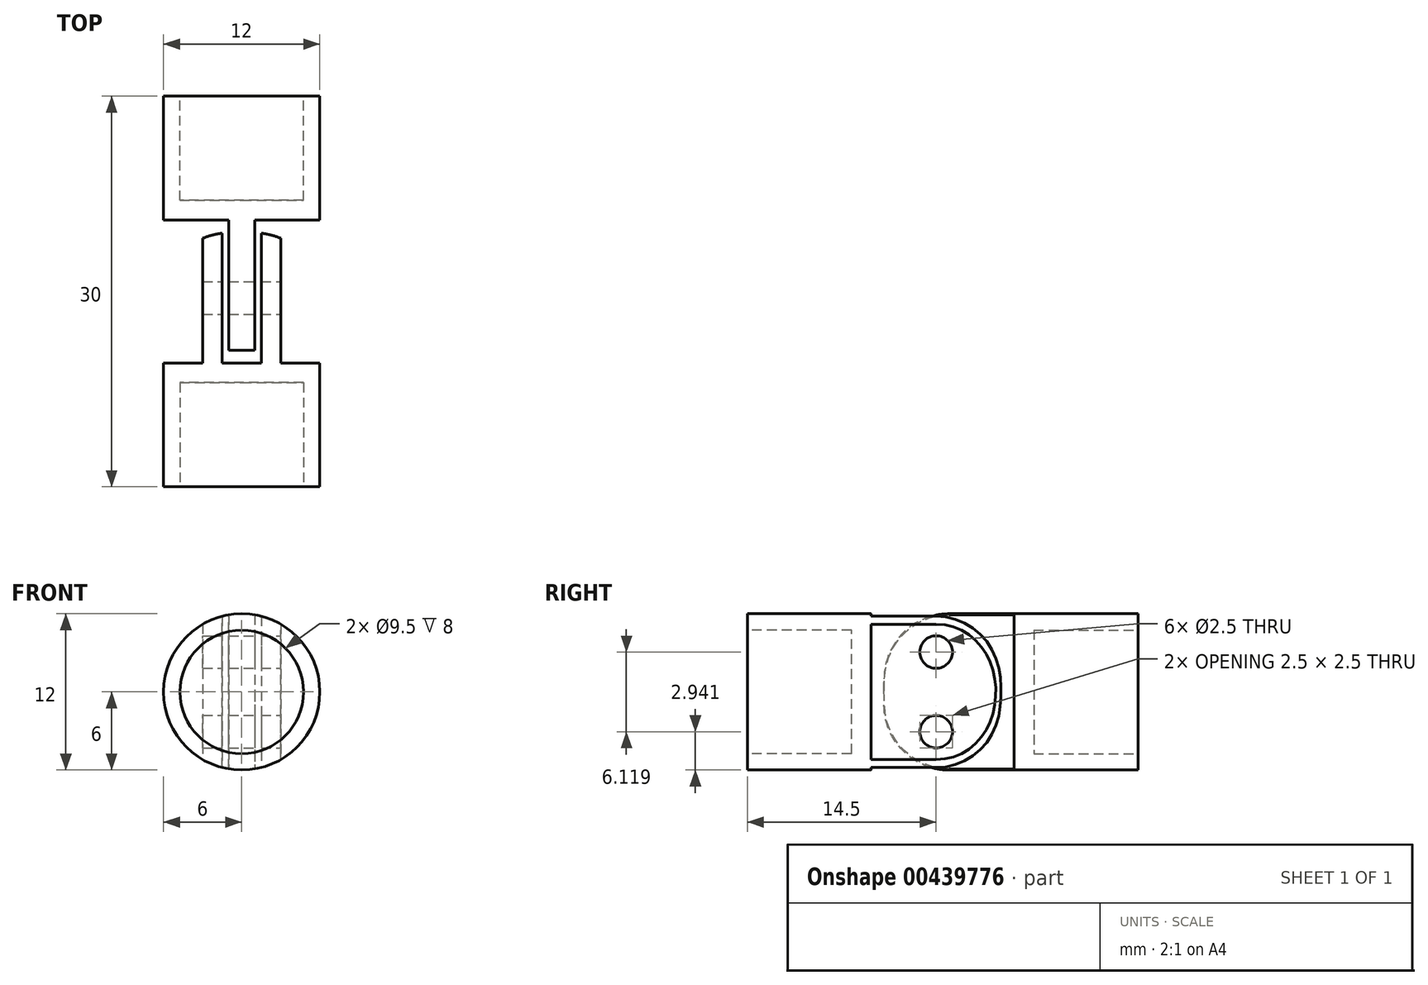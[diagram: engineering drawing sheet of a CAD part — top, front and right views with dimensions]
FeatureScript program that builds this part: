
annotation { "Feature Type Name" : "Feature", "Feature Type Description" : "" }
export const myFeature = defineFeature(function(context is Context, id is Id, definition is map)
    precondition{}
    {
        {
            var Q0;
            Q0=qCreatedBy(makeId("Top.planeOp"),FACE);
            var sketch = newSketch(context, id + "F0", { "sketchPlane" : qUnion([Q0])});
            skLineSegment(sketch, "E0.top", {"start": v(-6, -20.5) * mm, "end": v(6, -20.5) * mm});
            skLineSegment(sketch, "E0.left", {"start": v(-6, 9.5) * mm, "end": v(-6, 0) * mm});
            skLineSegment(sketch, "E0.right", {"start": v(6, 9.5) * mm, "end": v(6, 0) * mm});
            skLineSegment(sketch, "E1", {"start": v(-6, 0) * mm, "end": v(-1, 0) * mm});
            skLineSegment(sketch, "E2", {"start": v(-3, -1) * mm, "end": v(-1.5, -1) * mm});
            skLineSegment(sketch, "E3.trimOffspring", {"start": v(6, -11) * mm, "end": v(6, -20.5) * mm});
            skLineSegment(sketch, "E4.trimOffspring", {"start": v(-6, -11) * mm, "end": v(-6, -20.5) * mm});
            skLineSegment(sketch, "E5", {"start": v(-1, 0) * mm, "end": v(-1, -10) * mm});
            skLineSegment(sketch, "E6", {"start": v(-1, -10) * mm, "end": v(1, -10) * mm});
            skLineSegment(sketch, "E7", {"start": v(1, -10) * mm, "end": v(1, 0) * mm});
            skLineSegment(sketch, "E8", {"start": v(-1.5, -1) * mm, "end": v(-1.5, -11) * mm});
            skLineSegment(sketch, "E9", {"start": v(-1.5, -11) * mm, "end": v(1.5, -11) * mm});
            skLineSegment(sketch, "E10", {"start": v(1.5, -11) * mm, "end": v(1.5, -1) * mm});
            skLineSegment(sketch, "E11.trimOffspring", {"start": v(1.5, -1) * mm, "end": v(3, -1) * mm});
            skLineSegment(sketch, "E12", {"start": v(-3, -1) * mm, "end": v(-3, -11) * mm});
            skLineSegment(sketch, "E13", {"start": v(-3, -11) * mm, "end": v(-6, -11) * mm});
            skLineSegment(sketch, "E14", {"start": v(3, -1) * mm, "end": v(3, -11) * mm});
            skLineSegment(sketch, "E15", {"start": v(3, -11) * mm, "end": v(6, -11) * mm});
            skLineSegment(sketch, "E16.trimOffspring", {"start": v(1, 0) * mm, "end": v(6, 0) * mm});
            skLineSegment(sketch, "E17", {"start": v(-6, 9.5) * mm, "end": v(6, 9.5) * mm});
            skPoint(sketch, "E18.orphan", {"position": v(-6, 20) * mm});
            skSolve(sketch);
        }
        {
            var Q0;
            Q0=makeQuery(id+"F0.imprint","IMPRINT",FACE,{"disambiguationData":[TD([[makeQuery(id+"F0.imprint","IMPRINT",EDGE,{"derivedFrom":sQuery(id+"F0.wireOp",EDGE,"E0.left")}),1.0]])]});
            var Q1;
            Q1=makeQuery(id+"F0.imprint","IMPRINT",FACE,{"disambiguationData":[TD([[makeQuery(id+"F0.imprint","IMPRINT",EDGE,{"derivedFrom":sQuery(id+"F0.wireOp",EDGE,"E0.top")}),1.0]])]});
            extrude(context, id + "F1", {"entities" : qUnion([Q0, Q1]), "depth" : 12 * mm});
        }
        {
            var Q0;
            Q0=makeQuery(id+"F1.opExtrude","SWEPT_FACE",FACE,{"disambiguationData":[OSD([sQuery(id+"F0.wireOp",EDGE,"E0.top")])]});
            var sketch = newSketch(context, id + "F2", { "sketchPlane" : qUnion([Q0])});
            skCircle(sketch, "E19", {"center": v(0, 6) * mm, "radius": 6 * mm});
            skPoint(sketch, "E19.centerSnap0", {"position": v(0, 12) * mm});
            skLineSegment(sketch, "E20.bottom", {"start": v(-8.83, 13.69) * mm, "end": v(9.23, 13.69) * mm});
            skLineSegment(sketch, "E20.top", {"start": v(-8.83, -2.58) * mm, "end": v(9.23, -2.58) * mm});
            skLineSegment(sketch, "E20.left", {"start": v(-8.83, 13.69) * mm, "end": v(-8.83, -2.58) * mm});
            skLineSegment(sketch, "E20.right", {"start": v(9.23, 13.69) * mm, "end": v(9.23, -2.58) * mm});
            skSolve(sketch);
        }
        {
            var Q0;
            Q0=qSketchRegion(id+"F2",true);
            extrude(context, id + "F3", {"entities" : qUnion([Q0]), "operationType" : NewBodyOperationType.REMOVE, "oppositeDirection" : true, "depth" : 35.7 * mm});
        }
        {
            var Q0;
            Q0=makeQuery(id+"F1.opExtrude","SWEPT_FACE",FACE,{"disambiguationData":[OSD([sQuery(id+"F0.wireOp",EDGE,"E14")])]});
            var sketch = newSketch(context, id + "F4", { "sketchPlane" : qUnion([Q0])});
            skCircle(sketch, "E21", {"center": v(-6, 2.94) * mm, "radius": 1.25 * mm});
            skSolve(sketch);
        }
        {
            var Q0;
            Q0=makeQuery(id+"F4.imprint","IMPRINT",FACE,{"disambiguationData":[TD([[makeQuery(id+"F4.imprint","IMPRINT",EDGE,{"derivedFrom":sQuery(id+"F4.wireOp",EDGE,"E21")}),1.0]])]});
            extrude(context, id + "F5", {"entities" : qUnion([Q0]), "operationType" : NewBodyOperationType.REMOVE, "oppositeDirection" : true, "depth" : 25 * mm});
        }
        {
            var Q0;
            Q0=makeQuery(id+"F1.opExtrude","SWEPT_FACE",FACE,{"disambiguationData":[OSD([sQuery(id+"F0.wireOp",EDGE,"E0.top")])]});
            var sketch = newSketch(context, id + "F6", { "sketchPlane" : qUnion([Q0])});
            skCircle(sketch, "E22", {"center": v(0, 6) * mm, "radius": 4.75 * mm});
            skSolve(sketch);
        }
        {
            var Q0;
            Q0=makeQuery(id+"F6.imprint","IMPRINT",FACE,{"disambiguationData":[TD([[makeQuery(id+"F6.imprint","IMPRINT",EDGE,{"derivedFrom":sQuery(id+"F6.wireOp",EDGE,"E22")}),1.0]])]});
            extrude(context, id + "F7", {"entities" : qUnion([Q0]), "operationType" : NewBodyOperationType.REMOVE, "oppositeDirection" : true, "depth" : 8 * mm});
        }
        {
            var Q0;
            Q0=makeQuery(id+"F1.opExtrude","SWEPT_FACE",FACE,{"disambiguationData":[OSD([sQuery(id+"F0.wireOp",EDGE,"E17")])]});
            var sketch = newSketch(context, id + "F8", { "sketchPlane" : qUnion([Q0])});
            skCircle(sketch, "E23", {"center": v(0, 6) * mm, "radius": 4.75 * mm});
            skSolve(sketch);
        }
        {
            var Q0;
            Q0=makeQuery(id+"F8.imprint","IMPRINT",FACE,{"disambiguationData":[TD([[makeQuery(id+"F8.imprint","IMPRINT",EDGE,{"derivedFrom":sQuery(id+"F8.wireOp",EDGE,"E23")}),1.0]])]});
            extrude(context, id + "F9", {"entities" : qUnion([Q0]), "operationType" : NewBodyOperationType.REMOVE, "oppositeDirection" : true, "depth" : 8 * mm});
        }
        {
            var Q0;
            Q0=makeQuery(id+"F3.boolean.opBoolean","INTERSECT",EDGE,{"disambiguationData":[OD(1.0)],"derivedFrom":[makeQuery(id+"F1.opExtrude","SWEPT_FACE",FACE,{"disambiguationData":[OSD([sQuery(id+"F0.wireOp",EDGE,"E11.trimOffspring")])]}),makeQuery(id+"F3.opExtrude","SWEPT_FACE",FACE,{"disambiguationData":[OSD([sQuery(id+"F2.wireOp",EDGE,"E19")])]})]});
            var Q1;
            Q1=makeQuery(id+"F3.boolean.opBoolean","INTERSECT",EDGE,{"disambiguationData":[OD(1.0)],"derivedFrom":[makeQuery(id+"F1.opExtrude","SWEPT_FACE",FACE,{"disambiguationData":[OSD([sQuery(id+"F0.wireOp",EDGE,"E2")])]}),makeQuery(id+"F3.opExtrude","SWEPT_FACE",FACE,{"disambiguationData":[OSD([sQuery(id+"F2.wireOp",EDGE,"E19")])]})]});
            fillet(context, id + "F10", {"entities" : qUnion([Q0, Q1]), "radius" : 5 * mm, "tangentPropagation" : true, "allowEdgeOverflow" : false});
        }
        {
            var Q0;
            Q0=makeQuery(id+"F3.boolean.opBoolean","INTERSECT",EDGE,{"disambiguationData":[OD(1.0)],"derivedFrom":[makeQuery(id+"F1.opExtrude","SWEPT_FACE",FACE,{"disambiguationData":[OSD([sQuery(id+"F0.wireOp",EDGE,"E6")])]}),makeQuery(id+"F3.opExtrude","SWEPT_FACE",FACE,{"disambiguationData":[OSD([sQuery(id+"F2.wireOp",EDGE,"E19")])]})]});
            var Q1;
            Q1=makeQuery(id+"F3.boolean.opBoolean","INTERSECT",EDGE,{"disambiguationData":[OD(0.0)],"derivedFrom":[makeQuery(id+"F1.opExtrude","SWEPT_FACE",FACE,{"disambiguationData":[OSD([sQuery(id+"F0.wireOp",EDGE,"E6")])]}),makeQuery(id+"F3.opExtrude","SWEPT_FACE",FACE,{"disambiguationData":[OSD([sQuery(id+"F2.wireOp",EDGE,"E19")])]})]});
            fillet(context, id + "F11", {"entities" : qUnion([Q0, Q1]), "radius" : 5 * mm, "tangentPropagation" : true, "allowEdgeOverflow" : false});
        }
        {
            var Q0;
            Q0=makeQuery(id+"F1.opExtrude","SWEPT_FACE",FACE,{"disambiguationData":[OSD([sQuery(id+"F0.wireOp",EDGE,"E14")])]});
            var sketch = newSketch(context, id + "F12", { "sketchPlane" : qUnion([Q0])});
            skCircle(sketch, "E24", {"center": v(-6, 9.06) * mm, "radius": 1.25 * mm});
            skSolve(sketch);
        }
        {
            var Q0;
            Q0=makeQuery(id+"F12.imprint","IMPRINT",FACE,{"disambiguationData":[TD([[makeQuery(id+"F12.imprint","IMPRINT",EDGE,{"derivedFrom":sQuery(id+"F12.wireOp",EDGE,"E24")}),1.0]])]});
            extrude(context, id + "F13", {"entities" : qUnion([Q0]), "operationType" : NewBodyOperationType.REMOVE, "oppositeDirection" : true, "depth" : 15 * mm});
        }
    });
